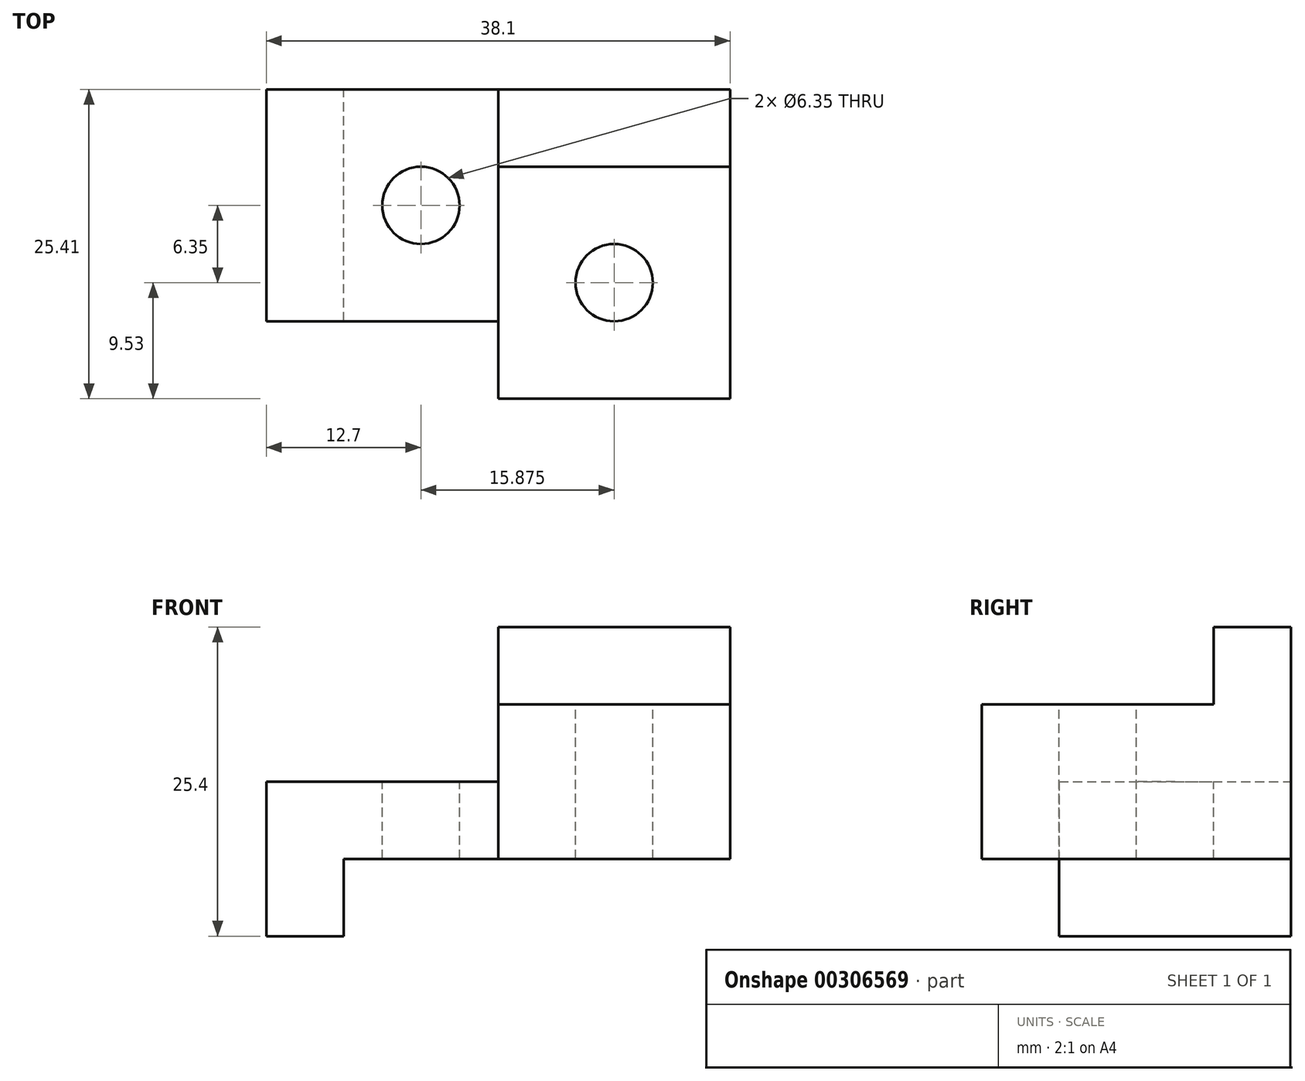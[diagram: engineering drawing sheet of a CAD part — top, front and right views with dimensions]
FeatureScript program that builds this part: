
annotation { "Feature Type Name" : "Feature", "Feature Type Description" : "" }
export const myFeature = defineFeature(function(context is Context, id is Id, definition is map)
    precondition{}
    {
        {
            var Q0;
            Q0=qCreatedBy(makeId("Front.planeOp"),FACE);
            var sketch = newSketch(context, id + "F0", { "sketchPlane" : qUnion([Q0])});
            skLineSegment(sketch, "E0", {"start": v(-19.05, -12.7) * mm, "end": v(-12.7, -12.7) * mm});
            skLineSegment(sketch, "E1", {"start": v(-12.7, -12.7) * mm, "end": v(-12.7, -6.35) * mm});
            skLineSegment(sketch, "E2", {"start": v(-12.7, -6.35) * mm, "end": v(19.05, -6.35) * mm});
            skLineSegment(sketch, "E3", {"start": v(19.05, -6.35) * mm, "end": v(19.05, 12.7) * mm});
            skLineSegment(sketch, "E4", {"start": v(19.05, 12.7) * mm, "end": v(0, 12.7) * mm});
            skLineSegment(sketch, "E5", {"start": v(0, 12.7) * mm, "end": v(0, 0) * mm});
            skLineSegment(sketch, "E6", {"start": v(0, 0) * mm, "end": v(-19.05, 0) * mm});
            skLineSegment(sketch, "E7", {"start": v(-19.05, 0) * mm, "end": v(-19.05, -12.7) * mm});
            skSolve(sketch);
        }
        {
            var Q0;
            Q0 = qSketchRegion(id + "F0", true);
            extrude(context, id + "F1", {"entities" : qUnion([Q0]), "endBound" : BoundingType.SYMMETRIC, "depth" : 19.05 * mm});
        }
        {
            var Q0;
            Q0=makeQuery(id+"F1.opExtrude","CAP_FACE",FACE,{"disambiguationData":[OSD([sQuery(id+"F0.wireOp",EDGE,"E0"),sQuery(id+"F0.wireOp",EDGE,"E1"),sQuery(id+"F0.wireOp",EDGE,"E2"),sQuery(id+"F0.wireOp",EDGE,"E3"),sQuery(id+"F0.wireOp",EDGE,"E4"),sQuery(id+"F0.wireOp",EDGE,"E5"),sQuery(id+"F0.wireOp",EDGE,"E6"),sQuery(id+"F0.wireOp",EDGE,"E7")])],"isStart":false});
            var sketch = newSketch(context, id + "F2", { "sketchPlane" : qUnion([Q0])});
            skLineSegment(sketch, "E8.bottom", {"start": v(19.05, -6.35) * mm, "end": v(0, -6.35) * mm});
            skLineSegment(sketch, "E8.top", {"start": v(19.05, 6.35) * mm, "end": v(0, 6.35) * mm});
            skLineSegment(sketch, "E8.left", {"start": v(19.05, -6.35) * mm, "end": v(19.05, 6.35) * mm});
            skLineSegment(sketch, "E8.right", {"start": v(0, -6.35) * mm, "end": v(0, 6.35) * mm});
            skSolve(sketch);
        }
        {
            var Q0;
            Q0 = qSketchRegion(id + "F2", true);
            extrude(context, id + "F3", {"entities" : qUnion([Q0]), "operationType" : NewBodyOperationType.ADD, "depth" : 6.35 * mm});
        }
        {
            var Q0;
            Q0=makeQuery(id+"F1.opExtrude","SWEPT_FACE",FACE,{"disambiguationData":[OSD([sQuery(id+"F0.wireOp",EDGE,"E4")])]});
            var sketch = newSketch(context, id + "F4", { "sketchPlane" : qUnion([Q0])});
            skLineSegment(sketch, "E9.bottom", {"start": v(0, -9.53) * mm, "end": v(19.05, -9.53) * mm});
            skLineSegment(sketch, "E9.top", {"start": v(0, 3.18) * mm, "end": v(19.05, 3.18) * mm});
            skLineSegment(sketch, "E9.left", {"start": v(0, -9.53) * mm, "end": v(0, 3.18) * mm});
            skLineSegment(sketch, "E9.right", {"start": v(19.05, -9.53) * mm, "end": v(19.05, 3.18) * mm});
            skSolve(sketch);
        }
        {
            var Q0;
            Q0 = qSketchRegion(id + "F4", true);
            extrude(context, id + "F5", {"entities" : qUnion([Q0]), "operationType" : NewBodyOperationType.REMOVE, "oppositeDirection" : true, "depth" : 6.35 * mm});
        }
        {
            var Q0;
            Q0=qCreatedBy(makeId("Top.planeOp"),FACE);
            var sketch = newSketch(context, id + "F6", { "sketchPlane" : qUnion([Q0])});
            skCircle(sketch, "E10", {"center": v(-6.35, 0) * mm, "radius": 3.18 * mm});
            skCircle(sketch, "E11", {"center": v(9.53, -6.35) * mm, "radius": 3.18 * mm});
            skSolve(sketch);
        }
        {
            var Q0;
            Q0 = qSketchRegion(id + "F6", true);
            extrude(context, id + "F7", {"entities" : qUnion([Q0]), "operationType" : NewBodyOperationType.REMOVE, "endBound" : BoundingType.THROUGH_ALL, "oppositeDirection" : true, "depth" : 25.4 * mm, "hasSecondDirection" : true, "secondDirectionOppositeDirection" : false, "secondDirectionDepth" : 25.4 * mm});
        }
    });
